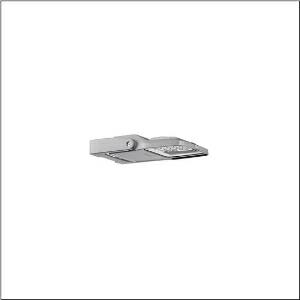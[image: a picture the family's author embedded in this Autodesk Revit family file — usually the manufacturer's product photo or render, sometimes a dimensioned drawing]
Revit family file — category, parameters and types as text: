
# Revit family: floodlight_fl_21_iq_micro___pl43_5xa7762a4a2a_306a
name_source: partatom
category: Lighting Fixtures
units: mm (PartAtom-declared; Revit-internal decimal feet)

## family parameters
Cut with Voids When Loaded = No
Host = Face
Light Source = No
Part Type = Normal
Room Calculation Point = No
Round Connector Dimension = Use Diameter
Shared = No

## types (1)
- --- (1 x LED, 3170 lm, 23.1 W, 4000K)
    Apparent Load = 23 VA
    CIE Flux Codes = 29 80 99 100 100
    Color Rendering = 70
    Color Temperature = 4000K
    Default Elevation = 1800 mm
    Description = Floodlight FL 21 iQ micro, floodlight, primary light control with lens, of PMMA, primary optical cover: protective disc, of toughened safety glass, transparent, light distribution: PL43, light emission: direct distribution, installation type: surface-mounted, LED, High Power LED, rated luminous flux: 3.170lm, luminous efficacy: 137lm/W, light colour: 740, colour temperature: 4000K, control gear: iQ Street-Remote/DALI, control: Auto-Match, Temp-Guard, Night-Set, Smart-Wire, Desk-Remote (wireless, voltage-free reading and setting of iQ features in the workshop via application-optimized NFC function/RFID function), optimised constant luminous flux control (CLO 2.0), Street-Remote, with terminal, 6-pole, mains connection: 220..240V, AC, 50/60Hz, start of lifetime: 23W, end of service life: 24W, reduction: 11W, luminaire housing, of diecast aluminium, powder-coated, Siteco® metallic grey (DB 702S), corrosivity category C5 mid according to DIN EN ISO 12944, suitable for swimming pools, chlorine-resistant, sealing non-destructively replaceable, design bracket, of diecast aluminium, powder-coated, Siteco® metallic grey (DB 702S), protection rating (complete): IP66, insulation class (complete): insulation class II (safety insulation), certification: CE, ENEC, VDE, protection symbol: D, impact resistance: IK07, permissible operating ambient temperature: -40..+40°C, permissible operating ambient temperature for outdoor applications: -40..+50°C, standard: DIN EN 12944, LABS conformity tested according to VDMA 24364:2018-05, packaging unit: 1 piece

Light Distribution: PL43
    Height = 65 mm
    Lamp = 1 x LED
    Lamp Light Flux = 3170 lm
    Lamp Power = 23.1 W
    Lamp count = 1
    Length = 312 mm
    Luminous efficacy = 137 lm/W
    Manufacturer = Siteco
    ModVariant = No
    Model = 5XA7762A4A2A
    Mounting Place = Wall
    Mounting Type = Surface mounted
    Number of Poles = 1
    OnlyDefault = Yes
    Power Factor = 1
    Product Name = Floodlight FL 21 iQ micro | PL43
    Product group = floodlight | wall mounted
    ProductGroupID = 2001
    Protection Class = Protection class II
    Protection Degree = IP 66
    RLX_Detail_Level = 1
    RLX_Emergency_Light_Flux = 0 lm
    RLX_Emergency_Type = 0
    RLX_Emergency_Type_DB = No
    RlxData = <blob elided: 97469 chars, md5=06fe2ef8>
    Socket = socket
    Standby Power = 0 W
    System Light Flux = 3170 lm
    System Power = 23 W
    Type Comments = factory setting: luminous flux: 100 % | dim-lin: 254 | 455 mA
    Type Image = l_1006878.jpg
    URL = http://relux.com
    VarID = @adj_197977
    Voltage = 0 V
    Weight = 0.00 kg
    Width = 230 mm

## geometry (parser evidence)
native form markers: Blend x4, Sweep x12
no freeform markers — native parametric forms only
